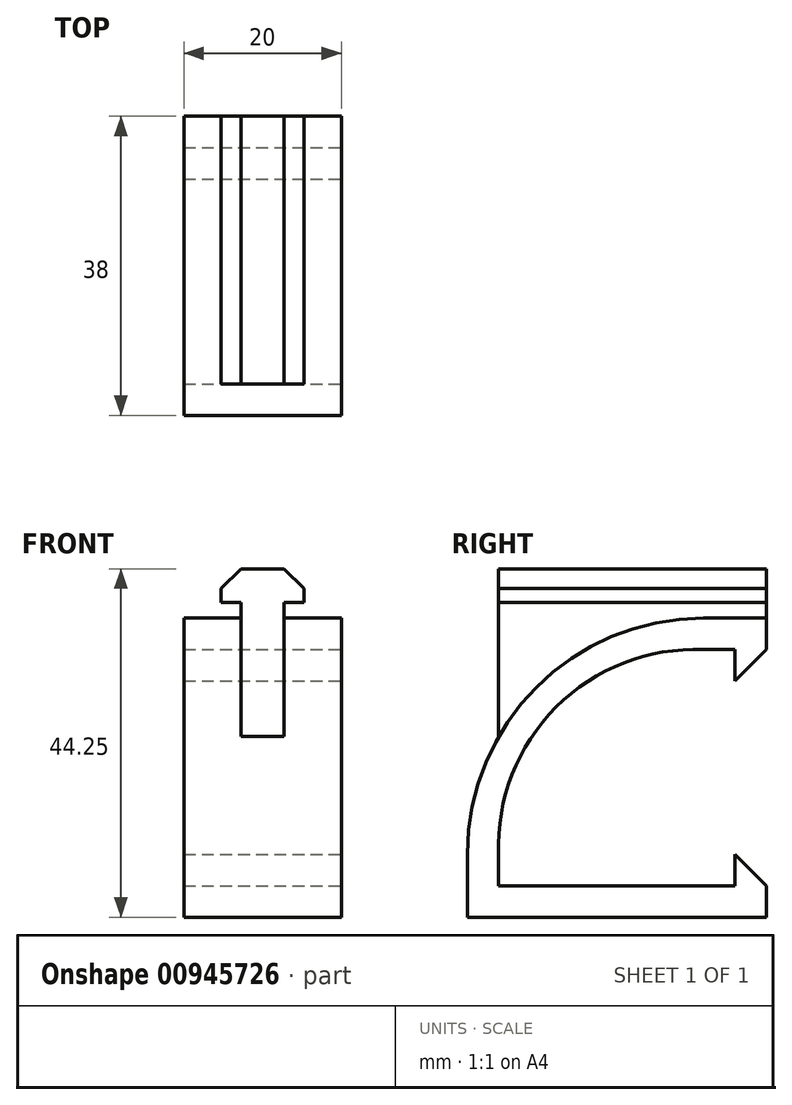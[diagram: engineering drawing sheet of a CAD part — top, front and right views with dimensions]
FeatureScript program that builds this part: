
annotation { "Feature Type Name" : "Feature", "Feature Type Description" : "" }
export const myFeature = defineFeature(function(context is Context, id is Id, definition is map)
    precondition{}
    {
        {
            var Q0;
            Q0=qCreatedBy(makeId("Right.planeOp"),FACE);
            var sketch = newSketch(context, id + "F0", { "sketchPlane" : qUnion([Q0])});
            skPoint(sketch, "E0", {"position": v(0, 0) * mm});
            skPoint(sketch, "E1", {"position": v(-30, 0) * mm});
            skLineSegment(sketch, "E2", {"start": v(-30, 0) * mm, "end": v(0, 0) * mm});
            skLineSegment(sketch, "E3", {"start": v(0, 0) * mm, "end": v(0, 4) * mm});
            skLineSegment(sketch, "E4", {"start": v(0, 4) * mm, "end": v(4, 0) * mm});
            skLineSegment(sketch, "E5", {"start": v(4, 0) * mm, "end": v(4, -4) * mm});
            skLineSegment(sketch, "E6", {"start": v(4, -4) * mm, "end": v(0, -4) * mm});
            skLineSegment(sketch, "E7", {"start": v(0, -4) * mm, "end": v(-30, -4) * mm});
            skLineSegment(sketch, "E8", {"start": v(-30, -4) * mm, "end": v(-34, -4) * mm});
            skLineSegment(sketch, "E9", {"start": v(-30, 0) * mm, "end": v(-30, 4) * mm});
            skPoint(sketch, "E10", {"position": v(0, 30) * mm});
            skLineSegment(sketch, "E11", {"start": v(0, 30) * mm, "end": v(-4, 30) * mm});
            skArc(sketch, "E12", {"start": v(-4, 30) * mm, "mid": v(-22.7, 22.7) * mm, "end": v(-30, 4) * mm});
            skLineSegment(sketch, "E13", {"start": v(-34, -4) * mm, "end": v(-34, 4) * mm});
            skLineSegment(sketch, "E14", {"start": v(0, 30) * mm, "end": v(0, 26) * mm});
            skLineSegment(sketch, "E15", {"start": v(0, 26) * mm, "end": v(4, 30) * mm});
            skLineSegment(sketch, "E16", {"start": v(4, 30) * mm, "end": v(4, 34) * mm});
            skLineSegment(sketch, "E17", {"start": v(4, 34) * mm, "end": v(0, 34) * mm});
            skLineSegment(sketch, "E18", {"start": v(0, 34) * mm, "end": v(-4, 34) * mm});
            skArc(sketch, "E19", {"start": v(-34, 4) * mm, "mid": v(-25.21, 25.21) * mm, "end": v(-4, 34) * mm});
            skSolve(sketch);
        }
        {
            var Q0;
            Q0=makeQuery(id+"F0.imprint","IMPRINT",FACE,{"disambiguationData":[TD([[makeQuery(id+"F0.imprint","IMPRINT",EDGE,{"derivedFrom":sQuery(id+"F0.wireOp",EDGE,"E2")}),-1.0]])]});
            extrude(context, id + "F1", {"entities" : qUnion([Q0]), "oppositeDirection" : true, "depth" : 10 * mm, "offsetDistance" : 25 * mm});
        }
        {
            var Q0;
            Q0=makeQuery(id+"F1.opExtrude","CAP_FACE",FACE,{"disambiguationData":[OSD([sQuery(id+"F0.wireOp",EDGE,"E2"),sQuery(id+"F0.wireOp",EDGE,"E3"),sQuery(id+"F0.wireOp",EDGE,"E4"),sQuery(id+"F0.wireOp",EDGE,"E5"),sQuery(id+"F0.wireOp",EDGE,"E6"),sQuery(id+"F0.wireOp",EDGE,"E7"),sQuery(id+"F0.wireOp",EDGE,"E8"),sQuery(id+"F0.wireOp",EDGE,"FjjRtSZg-fOcF-fDYo-Qgpg-al2X0iVIcEkg"),sQuery(id+"F0.wireOp",EDGE,"LCWHhztG-3RUY-vCQc-GlRJ-rhhH1wgmoH3L"),sQuery(id+"F0.wireOp",EDGE,"GnUkeDDz-5pcF-V5h8-9uln-NddxgMXTqBOd"),sQuery(id+"F0.wireOp",EDGE,"w3uFvqYJ-ilc1-WBBx-C5Oh-71L9XYVl8YLv"),sQuery(id+"F0.wireOp",EDGE,"L7J9hVKZ-CWtM-BNQ7-LR3i-usVN8eSDvRTx"),sQuery(id+"F0.wireOp",EDGE,"XAmmtVsw-YKKy-JudT-p935-uiNFMy5Iij6S")])],"isStart":true});
            extrude(context, id + "F2", {"entities" : qUnion([Q0]), "operationType" : NewBodyOperationType.ADD, "depth" : 10 * mm, "offsetDistance" : 25 * mm});
        }
        {
            var Q0;
            Q0=qCreatedBy(makeId("Front.planeOp"),FACE);
            var sketch = newSketch(context, id + "F3", { "sketchPlane" : qUnion([Q0])});
            skPoint(sketch, "E20", {"position": v(0, 0) * mm});
            skPoint(sketch, "E21", {"position": v(2.75, 34) * mm});
            skPoint(sketch, "E22", {"position": v(-2.75, 34) * mm});
            skLineSegment(sketch, "E23", {"start": v(2.75, 34) * mm, "end": v(2.75, 36) * mm});
            skLineSegment(sketch, "E24", {"start": v(2.75, 36) * mm, "end": v(-2.75, 36) * mm, "construction": true});
            skLineSegment(sketch, "E25", {"start": v(-2.75, 36) * mm, "end": v(-2.75, 34) * mm});
            skLineSegment(sketch, "E26", {"start": v(2.75, 36) * mm, "end": v(5.25, 36) * mm});
            skLineSegment(sketch, "E27", {"start": v(5.25, 36) * mm, "end": v(5.25, 37.75) * mm});
            skLineSegment(sketch, "E28", {"start": v(5.25, 37.75) * mm, "end": v(2.75, 40.25) * mm});
            skLineSegment(sketch, "E29", {"start": v(2.75, 40.25) * mm, "end": v(-2.75, 40.25) * mm});
            skLineSegment(sketch, "E30", {"start": v(-2.75, 40.25) * mm, "end": v(-5.25, 37.75) * mm});
            skLineSegment(sketch, "E31", {"start": v(-5.25, 37.75) * mm, "end": v(-5.25, 36) * mm});
            skLineSegment(sketch, "E32", {"start": v(-5.25, 36) * mm, "end": v(-2.75, 36) * mm});
            skPoint(sketch, "E33", {"position": v(0, 34) * mm});
            skPoint(sketch, "E33.positionSnap0", {"position": v(0, 36) * mm});
            skLineSegment(sketch, "E34", {"start": v(-2.75, 34) * mm, "end": v(0, 34) * mm});
            skLineSegment(sketch, "E35", {"start": v(2.75, 34) * mm, "end": v(0, 34) * mm});
            skSolve(sketch);
        }
        {
            var Q0;
            Q0=makeQuery(id+"F3.imprint","IMPRINT",FACE,{"disambiguationData":[TD([[makeQuery(id+"F3.imprint","IMPRINT",EDGE,{"derivedFrom":sQuery(id+"F3.wireOp",EDGE,"E23")}),1.0]])]});
            extrude(context, id + "F4", {"entities" : qUnion([Q0]), "operationType" : NewBodyOperationType.ADD, "depth" : 30 * mm, "offsetDistance" : 25 * mm});
        }
        {
            var Q0;
            Q0=makeQuery(id+"F4.opExtrude","CAP_FACE",FACE,{"disambiguationData":[OSD([sQuery(id+"F3.wireOp",EDGE,"bAfD1PQu-LIwF-rKrZ-XzKM-IWDmWgm2jqgU"),sQuery(id+"F3.wireOp",EDGE,"E23"),sQuery(id+"F3.wireOp",EDGE,"E25"),sQuery(id+"F3.wireOp",EDGE,"E26"),sQuery(id+"F3.wireOp",EDGE,"E27"),sQuery(id+"F3.wireOp",EDGE,"E28"),sQuery(id+"F3.wireOp",EDGE,"E29"),sQuery(id+"F3.wireOp",EDGE,"E30"),sQuery(id+"F3.wireOp",EDGE,"E31"),sQuery(id+"F3.wireOp",EDGE,"E32")])],"isStart":true});
            extrude(context, id + "F5", {"entities" : qUnion([Q0]), "operationType" : NewBodyOperationType.ADD, "depth" : 4 * mm, "offsetDistance" : 25 * mm});
        }
        {
            var Q0;
            Q0=makeQuery(id+"F4.opExtrude","SWEPT_FACE",FACE,{"disambiguationData":[OSD([sQuery(id+"F3.wireOp",EDGE,"E34"),sQuery(id+"F3.wireOp",EDGE,"E35")])]});
            extrude(context, id + "F6", {"entities" : qUnion([Q0]), "operationType" : NewBodyOperationType.ADD, "endBound" : BoundingType.UP_TO_NEXT, "depth" : 25 * mm, "offsetDistance" : 25 * mm});
        }
    });
